# Revit family: Furniture_Table_Spacestor_Breve Breakout Table
name_source: partatom
category: Furniture
revit_build: Autodesk Revit 2015 (Build: 20140223_1515(x64)
units: mm (PartAtom-declared; Revit-internal decimal feet)

## types (13) — shared parameters
Assembly Code = E2020200
Fabric Finish = <By Category>
Legs Finish = Spacestor Polished Steel
Length = 3000 mm  [stored 9.84252 ft]
Manufacturer = Spacestor
Table Top Finish = Spacestor White Table Top
URL = http://spacestor.uk.com

## per-type parameters (varying)
| type | Circular | Height | Leg Height | Square | Width |
| coffee height circular - 1000 DIA x 485h | Yes | 485 mm  [stored 1.59121 ft] | 310 mm  [stored 1.01706 ft] | No | 1000 mm  [stored 3.28084 ft] |
| standard height circular - 1000 DIA x 732h | Yes | 732 mm  [stored 2.40157 ft] | 557 mm | No | 1000 mm  [stored 3.28084 ft] |
| standard height square - 1000w x 1000d x 732h | No | 732 mm  [stored 2.40157 ft] | 557 mm | Yes | 1000 mm  [stored 3.28084 ft] |
| coffee height circular - 1100 DIA x 485h | Yes | 485 mm  [stored 1.59121 ft] | 310 mm  [stored 1.01706 ft] | No | 1100 mm |
| coffee height circular - 900 DIA x 485h | Yes | 485 mm  [stored 1.59121 ft] | 310 mm  [stored 1.01706 ft] | No | 900 mm  [stored 2.95276 ft] |
| coffee height square - 1000w x 1000d x 485h | No | 485 mm  [stored 1.59121 ft] | 310 mm  [stored 1.01706 ft] | Yes | 1000 mm  [stored 3.28084 ft] |
| coffee height square - 1100w x 1100d x 485h | No | 485 mm  [stored 1.59121 ft] | 310 mm  [stored 1.01706 ft] | Yes | 1100 mm |
| coffee height square - 900w x 900d x 485h | No | 485 mm  [stored 1.59121 ft] | 310 mm  [stored 1.01706 ft] | Yes | 900 mm  [stored 2.95276 ft] |
| standard height circular - 1100 DIA x 732h | Yes | 732 mm  [stored 2.40157 ft] | 557 mm | No | 1100 mm |
| standard height circular - 1200 DIA x 732h | Yes | 732 mm  [stored 2.40157 ft] | 557 mm | No | 1200 mm  [stored 3.93701 ft] |
| standard height circular - 1400 DIA x 732h | Yes | 732 mm  [stored 2.40157 ft] | 557 mm | No | 1400 mm  [stored 4.59318 ft] |
| standard height square - 1100w x 1100d x 732h | No | 732 mm  [stored 2.40157 ft] | 557 mm | Yes | 1100 mm |
| standard height square - 1200w x 1200d x 732h | No | 732 mm  [stored 2.40157 ft] | 557 mm | Yes | 1200 mm  [stored 3.93701 ft] |

note: [stored X ft] marks values corroborated as IEEE doubles in the binary element streams (Revit-internal decimal feet)

## geometry (parser evidence)
native form markers: Sweep x39
no freeform markers — native parametric forms only
